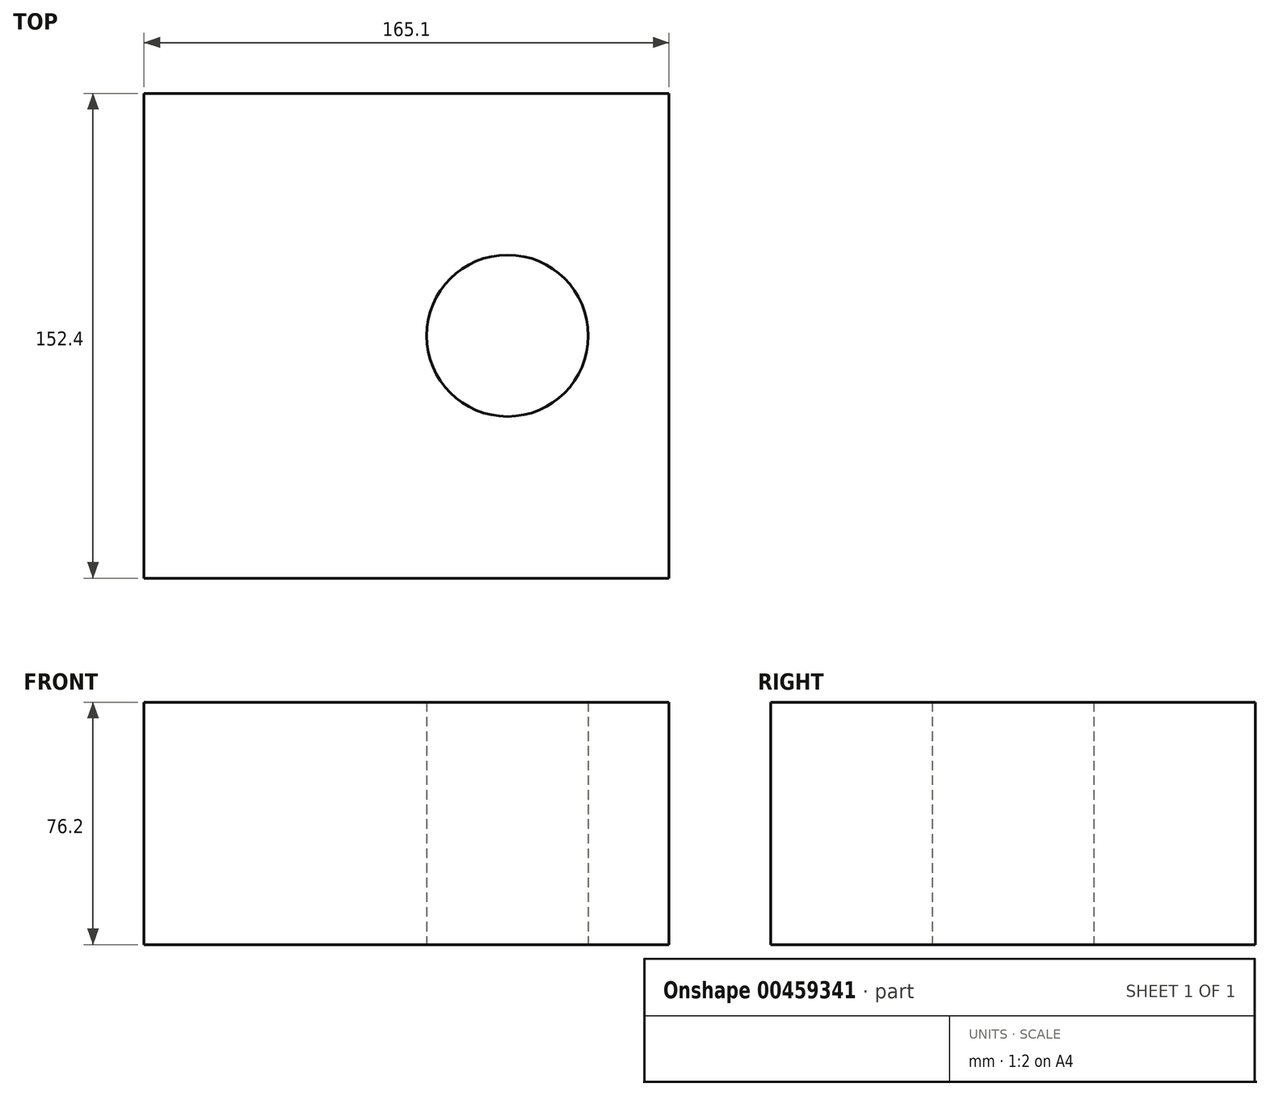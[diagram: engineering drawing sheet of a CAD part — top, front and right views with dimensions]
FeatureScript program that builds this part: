
annotation { "Feature Type Name" : "Feature", "Feature Type Description" : "" }
export const myFeature = defineFeature(function(context is Context, id is Id, definition is map)
    precondition{}
    {
        {
            var Q0;
            Q0=qCreatedBy(makeId("Front.planeOp"),FACE);
            var sketch = newSketch(context, id + "F0", { "sketchPlane" : qUnion([Q0])});
            skLineSegment(sketch, "E0.bottom", {"start": v(-114.3, 76.2) * mm, "end": v(114.3, 76.2) * mm});
            skLineSegment(sketch, "E0.top", {"start": v(-114.3, -76.2) * mm, "end": v(114.3, -76.2) * mm});
            skLineSegment(sketch, "E0.left", {"start": v(-114.3, 76.2) * mm, "end": v(-114.3, -76.2) * mm});
            skLineSegment(sketch, "E0.right", {"start": v(114.3, 76.2) * mm, "end": v(114.3, -76.2) * mm});
            skPoint(sketch, "E0.middle", {"position": v(0, 0) * mm});
            skLineSegment(sketch, "E1.bottom", {"start": v(114.3, 76.2) * mm, "end": v(-50.8, 76.2) * mm});
            skLineSegment(sketch, "E1.top", {"start": v(114.3, 0) * mm, "end": v(-50.8, 0) * mm});
            skLineSegment(sketch, "E1.left", {"start": v(114.3, 76.2) * mm, "end": v(114.3, 0) * mm});
            skLineSegment(sketch, "E1.right", {"start": v(-50.8, 76.2) * mm, "end": v(-50.8, 0) * mm});
            skSolve(sketch);
        }
        {
            var Q0;
            Q0=makeQuery(id+"F0.imprint","IMPRINT",FACE,{"disambiguationData":[TD([[makeQuery(id+"F0.imprint","IMPRINT",EDGE,{"derivedFrom":sQuery(id+"F0.wireOp",EDGE,"E0.bottom")}),-1.0]])]});
            extrude(context, id + "F1", {"entities" : qUnion([Q0]), "endBound" : BoundingType.SYMMETRIC, "depth" : 152.4 * mm});
        }
        {
            var Q0;
            Q0=makeQuery(id+"F1.opExtrude","SWEPT_FACE",FACE,{"disambiguationData":[OSD([sQuery(id+"F0.wireOp",EDGE,"E1.top")])]});
            var sketch = newSketch(context, id + "F2", { "sketchPlane" : qUnion([Q0])});
            skPoint(sketch, "E2", {"position": v(63.5, 0) * mm});
            skSolve(sketch);
        }
        {
            var Q0;
            Q0=sQuery(id+"F2.wireOp",VERTEX,"E2");
            var Q1;
            Q1=makeQuery(id+"F1.opExtrude","SWEPT_BODY",BODY,{"disambiguationData":[OSD([sQuery(id+"F0.wireOp",EDGE,"E0.bottom"),sQuery(id+"F0.wireOp",EDGE,"E0.top"),sQuery(id+"F0.wireOp",EDGE,"E0.left"),sQuery(id+"F0.wireOp",EDGE,"E0.right"),sQuery(id+"F0.wireOp",EDGE,"E1.top"),sQuery(id+"F0.wireOp",EDGE,"E1.right")])]});
            hole(context, id + "F3", {"style" : HoleStyle.SIMPLE, "endStyle" : HoleEndStyle.THROUGH, "holeDiameter" : 50.8 * mm, "isTappedThrough" : true, "tappedDepth" : 12.7 * mm, "tapClearance" : 3, "locations" : qUnion([Q0]), "scope" : qUnion([Q1])});
        }
    });
